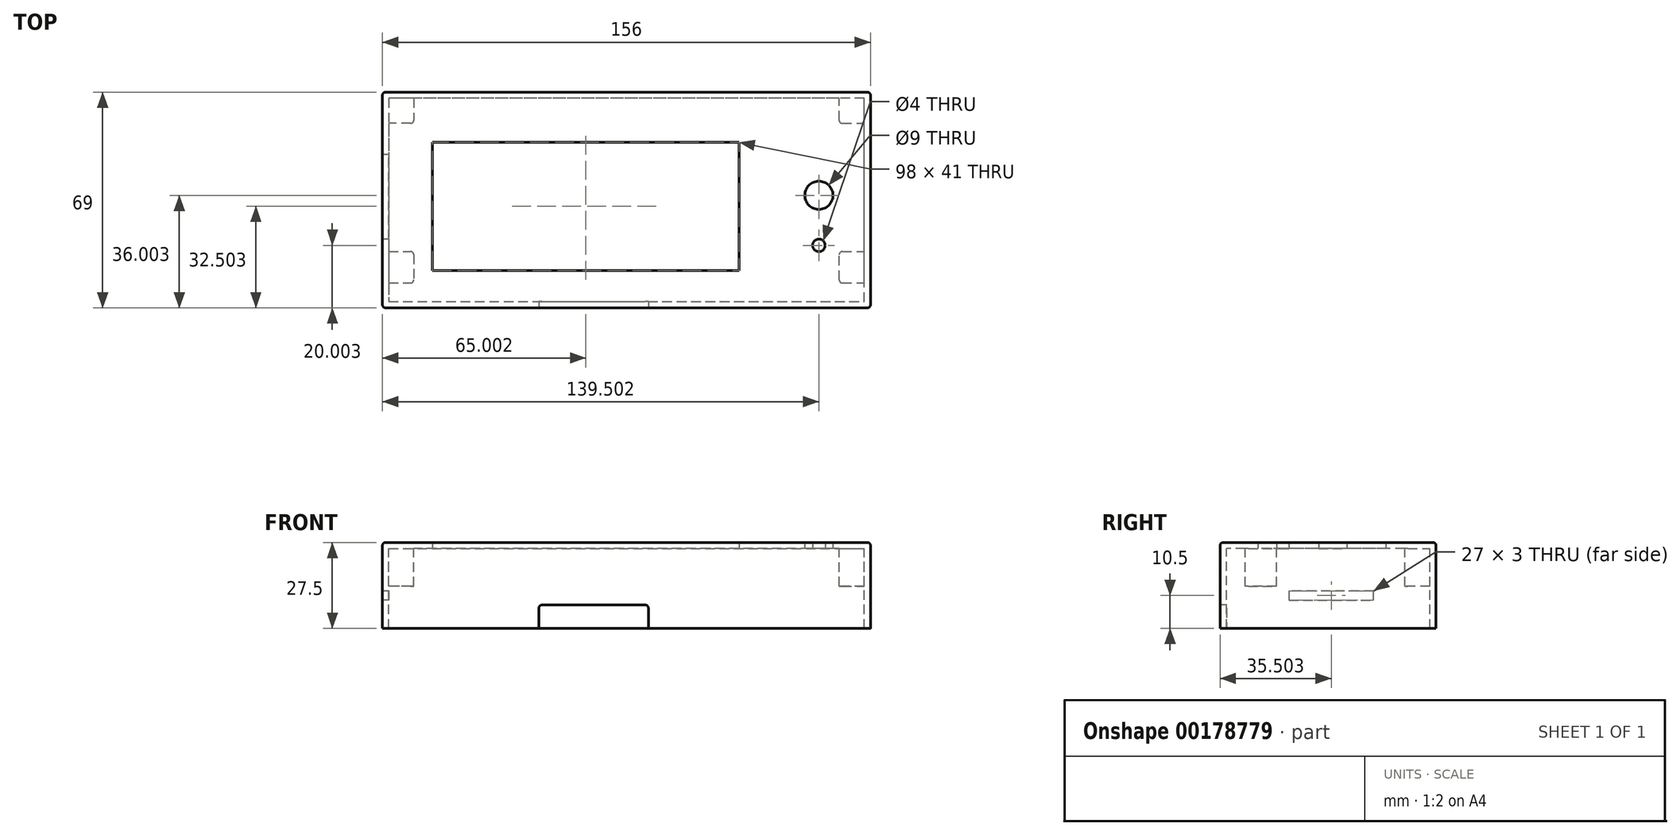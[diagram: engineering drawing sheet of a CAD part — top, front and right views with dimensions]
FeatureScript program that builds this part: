
annotation { "Feature Type Name" : "Feature", "Feature Type Description" : "" }
export const myFeature = defineFeature(function(context is Context, id is Id, definition is map)
    precondition{}
    {
        {
            var Q0;
            Q0=qCreatedBy(makeId("Top.planeOp"),FACE);
            var sketch = newSketch(context, id + "F0", { "sketchPlane" : qUnion([Q0])});
            skLineSegment(sketch, "E0.0", {"start": v(87.7, -27.77) * mm, "end": v(87.7, 35.23) * mm, "construction": true});
            skPoint(sketch, "E1.centerSnap0", {"position": v(87.7, 3.73) * mm});
            skLineSegment(sketch, "E2.0", {"start": v(101.2, 15.23) * mm, "end": v(-48.8, 15.23) * mm, "construction": true});
            skLineSegment(sketch, "E3.0", {"start": v(101.2, -11.77) * mm, "end": v(-48.8, -11.77) * mm, "construction": true});
            skLineSegment(sketch, "E4.0", {"start": v(62.2, 22.23) * mm, "end": v(-35.8, 22.23) * mm});
            skLineSegment(sketch, "E4.1", {"start": v(62.2, -18.77) * mm, "end": v(62.2, 22.23) * mm});
            skLineSegment(sketch, "E4.2", {"start": v(-35.8, -18.77) * mm, "end": v(62.2, -18.77) * mm});
            skLineSegment(sketch, "E4.3", {"start": v(-35.8, 22.23) * mm, "end": v(-35.8, -18.77) * mm});
            skLineSegment(sketch, "E5.0", {"start": v(102.2, 36.23) * mm, "end": v(-49.8, 36.23) * mm});
            skLineSegment(sketch, "E5.1", {"start": v(102.2, -28.77) * mm, "end": v(102.2, 36.23) * mm});
            skLineSegment(sketch, "E5.2", {"start": v(-49.8, -28.77) * mm, "end": v(102.2, -28.77) * mm});
            skLineSegment(sketch, "E5.3", {"start": v(-49.8, 36.23) * mm, "end": v(-49.8, -28.77) * mm});
            skLineSegment(sketch, "E6", {"start": v(87.7, 5.23) * mm, "end": v(102.2, 5.23) * mm, "construction": true});
            skLineSegment(sketch, "E7.0", {"start": v(87.7, -10.77) * mm, "end": v(102.2, -10.77) * mm, "construction": true});
            skCircle(sketch, "E8", {"center": v(87.7, -10.77) * mm, "radius": 2 * mm});
            skLineSegment(sketch, "E9.0", {"start": v(104.2, 38.23) * mm, "end": v(-51.8, 38.23) * mm});
            skLineSegment(sketch, "E9.1", {"start": v(104.2, -30.77) * mm, "end": v(104.2, 38.23) * mm});
            skLineSegment(sketch, "E9.2", {"start": v(-51.8, -30.77) * mm, "end": v(104.2, -30.77) * mm});
            skLineSegment(sketch, "E9.3", {"start": v(-51.8, 38.23) * mm, "end": v(-51.8, -30.77) * mm});
            skLineSegment(sketch, "E10.0", {"start": v(-43.8, -12.77) * mm, "end": v(96.2, -12.77) * mm, "construction": true});
            skLineSegment(sketch, "E11.0", {"start": v(96.2, 30.23) * mm, "end": v(-43.8, 30.23) * mm, "construction": true});
            skLineSegment(sketch, "E12", {"start": v(96.2, -12.77) * mm, "end": v(102.2, -12.77) * mm});
            skLineSegment(sketch, "E13", {"start": v(-49.8, -12.77) * mm, "end": v(-43.8, -12.77) * mm});
            skLineSegment(sketch, "E14.0", {"start": v(94.2, 28.23) * mm, "end": v(94.2, 36.23) * mm});
            skLineSegment(sketch, "E14.1", {"start": v(94.2, 28.23) * mm, "end": v(102.2, 28.23) * mm});
            skLineSegment(sketch, "E15.0", {"start": v(94.2, -22.77) * mm, "end": v(94.2, -12.77) * mm});
            skLineSegment(sketch, "E16", {"start": v(96.2, -12.77) * mm, "end": v(94.2, -12.77) * mm});
            skLineSegment(sketch, "E17.0", {"start": v(96.2, -22.77) * mm, "end": v(102.2, -22.77) * mm});
            skLineSegment(sketch, "E18.trimOffspring", {"start": v(94.2, -22.77) * mm, "end": v(96.2, -22.77) * mm});
            skLineSegment(sketch, "E19.0", {"start": v(-41.8, -12.77) * mm, "end": v(-41.8, -22.77) * mm});
            skLineSegment(sketch, "E20.0", {"start": v(-49.8, -22.77) * mm, "end": v(-43.8, -22.77) * mm});
            skLineSegment(sketch, "E21", {"start": v(-43.8, -12.77) * mm, "end": v(-41.8, -12.77) * mm});
            skLineSegment(sketch, "E22", {"start": v(-43.8, -22.77) * mm, "end": v(-41.8, -22.77) * mm});
            skLineSegment(sketch, "E23.0", {"start": v(-41.8, 28.23) * mm, "end": v(-49.8, 28.23) * mm});
            skLineSegment(sketch, "E23.1", {"start": v(-41.8, 36.23) * mm, "end": v(-41.8, 28.23) * mm});
            skCircle(sketch, "E24", {"center": v(87.7, 5.23) * mm, "radius": 4.5 * mm});
            skSolve(sketch);
        }
        {
            var Q0;
            Q0=makeQuery(id+"F0.imprint","IMPRINT",FACE,{"disambiguationData":[TD([[makeQuery(id+"F0.imprint","IMPRINT",EDGE,{"derivedFrom":sQuery(id+"F0.wireOp",EDGE,"E1")}),-1.0]])]});
            var Q1;
            {var subQ0=sQuery(id+"F0.wireOp",EDGE,"E5.3");Q1=makeQuery(id+"F0.imprint","IMPRINT",FACE,{"disambiguationData":[TD([[makeQuery(id+"F0.imprint","IMPRINT",EDGE,{"derivedFrom":subQ0}),1.0]])]});}
            var Q2;
            {var subQ0=sQuery(id+"F0.wireOp",EDGE,"E5.1");Q2=makeQuery(id+"F0.imprint","IMPRINT",FACE,{"disambiguationData":[TD([[makeQuery(id+"F0.imprint","IMPRINT",EDGE,{"derivedFrom":subQ0}),1.0]])]});}
            var Q3;
            {var subQ0=sQuery(id+"F0.wireOp",EDGE,"E5.1");Q3=makeQuery(id+"F0.imprint","IMPRINT",FACE,{"disambiguationData":[TD([[makeQuery(id+"F0.imprint","IMPRINT",EDGE,{"derivedFrom":subQ0}),-1.0]])]});}
            var Q4;
            {var subQ1=sQuery(id+"F0.wireOp",EDGE,"E13");Q4=makeQuery(id+"F0.imprint","IMPRINT",FACE,{"disambiguationData":[TD([[makeQuery(id+"F0.imprint","IMPRINT",EDGE,{"derivedFrom":subQ1}),-1.0]])]});}
            var Q5;
            {var subQ4=sQuery(id+"F0.wireOp",EDGE,"E23.0");Q5=makeQuery(id+"F0.imprint","IMPRINT",FACE,{"disambiguationData":[TD([[makeQuery(id+"F0.imprint","IMPRINT",EDGE,{"derivedFrom":subQ4}),-1.0]])]});}
            var Q6;
            {var subQ3=sQuery(id+"F0.wireOp",EDGE,"E14.0");Q6=makeQuery(id+"F0.imprint","IMPRINT",FACE,{"disambiguationData":[TD([[makeQuery(id+"F0.imprint","IMPRINT",EDGE,{"derivedFrom":subQ3}),-1.0]])]});}
            var Q7;
            {var subQ0=sQuery(id+"F0.wireOp",EDGE,"E12");Q7=makeQuery(id+"F0.imprint","IMPRINT",FACE,{"disambiguationData":[TD([[makeQuery(id+"F0.imprint","IMPRINT",EDGE,{"derivedFrom":subQ0}),-1.0]])]});}
            extrude(context, id + "F1", {"entities" : qUnion([Q0, Q1, Q2, Q3, Q4, Q5, Q6, Q7]), "depth" : 2 * mm});
        }
        {
            var Q0;
            {var subQ5=sQuery(id+"F0.wireOp",EDGE,"LqWD2sNj-Lfw8-2JLi-mVoA-2MaUUUqoJ69t");Q0=makeQuery(id+"F0.imprint","IMPRINT",FACE,{"disambiguationData":[TD([[makeQuery(id+"F0.imprint","IMPRINT",EDGE,{"derivedFrom":subQ5}),1.0]])]});}
            var Q1;
            {var subQ3=sQuery(id+"F0.wireOp",EDGE,"E12");Q1=makeQuery(id+"F0.imprint","IMPRINT",FACE,{"disambiguationData":[TD([[makeQuery(id+"F0.imprint","IMPRINT",EDGE,{"derivedFrom":subQ3}),-1.0]])]});}
            var Q2;
            {var subQ5=sQuery(id+"F0.wireOp",EDGE,"E13");Q2=makeQuery(id+"F0.imprint","IMPRINT",FACE,{"disambiguationData":[TD([[makeQuery(id+"F0.imprint","IMPRINT",EDGE,{"derivedFrom":subQ5}),-1.0]])]});}
            var Q3;
            {var subQ5=sQuery(id+"F0.wireOp",EDGE,"ybuCfW5r-dQPt-GAAb-xabZ-S6rsIlaVohmJ");Q3=makeQuery(id+"F0.imprint","IMPRINT",FACE,{"disambiguationData":[TD([[makeQuery(id+"F0.imprint","IMPRINT",EDGE,{"derivedFrom":subQ5}),-1.0]])]});}
            var Q4;
            {var subQ4=sQuery(id+"F0.wireOp",EDGE,"E23.0");Q4=makeQuery(id+"F0.imprint","IMPRINT",FACE,{"disambiguationData":[TD([[makeQuery(id+"F0.imprint","IMPRINT",EDGE,{"derivedFrom":subQ4}),-1.0]])]});}
            var Q5;
            {var subQ3=sQuery(id+"F0.wireOp",EDGE,"E14.0");Q5=makeQuery(id+"F0.imprint","IMPRINT",FACE,{"disambiguationData":[TD([[makeQuery(id+"F0.imprint","IMPRINT",EDGE,{"derivedFrom":subQ3}),-1.0]])]});}
            extrude(context, id + "F2", {"entities" : qUnion([Q0, Q1, Q2, Q3, Q4, Q5]), "operationType" : NewBodyOperationType.ADD, "oppositeDirection" : true, "depth" : (14 - 2) * mm});
        }
        {
            var Q0;
            Q0=makeQuery(id+"F0.imprint","IMPRINT",FACE,{"disambiguationData":[TD([[makeQuery(id+"F0.imprint","IMPRINT",EDGE,{"derivedFrom":sQuery(id+"F0.wireOp",EDGE,"E9.0")}),1.0]])]});
            extrude(context, id + "F3", {"entities" : qUnion([Q0]), "operationType" : NewBodyOperationType.ADD, "oppositeDirection" : true, "depth" : (15.5 + 10) * mm});
        }
        {
            var Q0;
            {var subQ0=sQuery(id+"F0.wireOp",EDGE,"E9.3");Q0=makeQuery(id+"F3.boolean.opBoolean","MERGE",FACE,{"derivedFrom":[makeQuery(id+"F1.opExtrude","SWEPT_FACE",FACE,{"disambiguationData":[OSD([subQ0])]}),makeQuery(id+"F3.opExtrude","SWEPT_FACE",FACE,{"disambiguationData":[OSD([subQ0])]})]});}
            var sketch = newSketch(context, id + "F4", { "sketchPlane" : qUnion([Q0])});
            skLineSegment(sketch, "E25.0", {"start": v(-18.23, 2) * mm, "end": v(-18.23, -25.5) * mm, "construction": true});
            skLineSegment(sketch, "E26.0", {"start": v(8.77, 2) * mm, "end": v(8.77, -25.5) * mm, "construction": true});
            skLineSegment(sketch, "E27.0", {"start": v(-38.23, -13.5) * mm, "end": v(30.77, -13.5) * mm, "construction": true});
            skLineSegment(sketch, "E28", {"start": v(-18.23, -13.5) * mm, "end": v(8.77, -13.5) * mm});
            skLineSegment(sketch, "E29", {"start": v(8.77, -13.5) * mm, "end": v(8.77, -16.5) * mm});
            skLineSegment(sketch, "E30", {"start": v(8.77, -16.5) * mm, "end": v(-18.23, -16.5) * mm});
            skLineSegment(sketch, "E31", {"start": v(-18.23, -16.5) * mm, "end": v(-18.23, -13.5) * mm});
            skLineSegment(sketch, "E32.top", {"start": v(-18.23, -16.5) * mm, "end": v(8.77, -16.5) * mm});
            skLineSegment(sketch, "E32.left", {"start": v(-18.23, -13.5) * mm, "end": v(-18.23, -16.5) * mm});
            skSolve(sketch);
        }
        {
            var Q0;
            Q0=makeQuery(id+"F4.imprint","IMPRINT",FACE,{"disambiguationData":[TD([[makeQuery(id+"F4.imprint","IMPRINT",EDGE,{"derivedFrom":sQuery(id+"F4.wireOp",EDGE,"E28")}),-1.0]])]});
            extrude(context, id + "F5", {"entities" : qUnion([Q0]), "operationType" : NewBodyOperationType.REMOVE, "oppositeDirection" : true, "depth" : 2 * mm});
        }
        {
            var Q0;
            {var subQ0=sQuery(id+"F0.wireOp",EDGE,"E9.2");Q0=makeQuery(id+"F3.boolean.opBoolean","MERGE",FACE,{"derivedFrom":[makeQuery(id+"F1.opExtrude","SWEPT_FACE",FACE,{"disambiguationData":[OSD([subQ0])]}),makeQuery(id+"F3.opExtrude","SWEPT_FACE",FACE,{"disambiguationData":[OSD([subQ0])]})]});}
            var sketch = newSketch(context, id + "F6", { "sketchPlane" : qUnion([Q0])});
            skLineSegment(sketch, "E33.0", {"start": v(-1.8, 2) * mm, "end": v(-1.8, -25.5) * mm, "construction": true});
            skLineSegment(sketch, "E34.0", {"start": v(33.2, 2) * mm, "end": v(33.2, -25.5) * mm, "construction": true});
            skLineSegment(sketch, "E35.0", {"start": v(-51.8, -18) * mm, "end": v(104.2, -18) * mm, "construction": true});
            skLineSegment(sketch, "E36.bottom", {"start": v(-1.8, -18) * mm, "end": v(33.2, -18) * mm});
            skLineSegment(sketch, "E36.top", {"start": v(-1.8, -25.5) * mm, "end": v(33.2, -25.5) * mm});
            skLineSegment(sketch, "E36.left", {"start": v(-1.8, -18) * mm, "end": v(-1.8, -25.5) * mm});
            skLineSegment(sketch, "E36.right", {"start": v(33.2, -18) * mm, "end": v(33.2, -25.5) * mm});
            skSolve(sketch);
        }
        {
            var Q0;
            Q0=makeQuery(id+"F6.imprint","IMPRINT",FACE,{"disambiguationData":[TD([[makeQuery(id+"F6.imprint","IMPRINT",EDGE,{"derivedFrom":sQuery(id+"F6.wireOp",EDGE,"E36.bottom")}),-1.0]])]});
            extrude(context, id + "F7", {"entities" : qUnion([Q0]), "operationType" : NewBodyOperationType.REMOVE, "oppositeDirection" : true, "depth" : 2 * mm});
        }
        {
            var Q0;
            {var subQ0=sQuery(id+"F0.wireOp",EDGE,"E9.3");var subQ1=sQuery(id+"F0.wireOp",EDGE,"E9.2");Q0=makeQuery(id+"F3.boolean.opBoolean","MERGE",EDGE,{"derivedFrom":[makeQuery(id+"F1.opExtrude","SWEPT_EDGE",EDGE,{"disambiguationData":[OSD([subQ1,subQ0])]}),makeQuery(id+"F3.opExtrude","SWEPT_EDGE",EDGE,{"disambiguationData":[OSD([subQ1,subQ0])]})]});}
            var Q1;
            Q1=makeQuery(id+"F1.opExtrude","CAP_EDGE",EDGE,{"disambiguationData":[OSD([sQuery(id+"F0.wireOp",EDGE,"E9.2")])],"isStart":false});
            var Q2;
            {var subQ0=sQuery(id+"F0.wireOp",EDGE,"E9.2");var subQ1=sQuery(id+"F0.wireOp",EDGE,"E9.1");Q2=makeQuery(id+"F3.boolean.opBoolean","MERGE",EDGE,{"derivedFrom":[makeQuery(id+"F1.opExtrude","SWEPT_EDGE",EDGE,{"disambiguationData":[OSD([subQ1,subQ0])]}),makeQuery(id+"F3.opExtrude","SWEPT_EDGE",EDGE,{"disambiguationData":[OSD([subQ1,subQ0])]})]});}
            var Q3;
            Q3=makeQuery(id+"F1.opExtrude","CAP_EDGE",EDGE,{"disambiguationData":[OSD([sQuery(id+"F0.wireOp",EDGE,"E9.1")])],"isStart":false});
            var Q4;
            {var subQ0=sQuery(id+"F0.wireOp",EDGE,"E9.1");var subQ1=sQuery(id+"F0.wireOp",EDGE,"E9.0");Q4=makeQuery(id+"F3.boolean.opBoolean","MERGE",EDGE,{"derivedFrom":[makeQuery(id+"F1.opExtrude","SWEPT_EDGE",EDGE,{"disambiguationData":[OSD([subQ1,subQ0])]}),makeQuery(id+"F3.opExtrude","SWEPT_EDGE",EDGE,{"disambiguationData":[OSD([subQ1,subQ0])]})]});}
            var Q5;
            Q5=makeQuery(id+"F1.opExtrude","CAP_EDGE",EDGE,{"disambiguationData":[OSD([sQuery(id+"F0.wireOp",EDGE,"E9.0")])],"isStart":false});
            var Q6;
            {var subQ0=sQuery(id+"F0.wireOp",EDGE,"E9.3");var subQ1=sQuery(id+"F0.wireOp",EDGE,"E9.0");Q6=makeQuery(id+"F3.boolean.opBoolean","MERGE",EDGE,{"derivedFrom":[makeQuery(id+"F1.opExtrude","SWEPT_EDGE",EDGE,{"disambiguationData":[OSD([subQ1,subQ0])]}),makeQuery(id+"F3.opExtrude","SWEPT_EDGE",EDGE,{"disambiguationData":[OSD([subQ1,subQ0])]})]});}
            var Q7;
            Q7=makeQuery(id+"F2.opExtrude","SWEPT_EDGE",EDGE,{"disambiguationData":[OSD([sQuery(id+"F0.wireOp",EDGE,"d95ecad5-aaf0-46ce-bc26-c3553d7e4dae.0"),sQuery(id+"F0.wireOp",EDGE,"ybuCfW5r-dQPt-GAAb-xabZ-S6rsIlaVohmJ")])]});
            var Q8;
            Q8=makeQuery(id+"F2.opExtrude","SWEPT_EDGE",EDGE,{"disambiguationData":[OSD([sQuery(id+"F0.wireOp",EDGE,"ea918c8d-915d-4296-b256-6586ec142c67.0"),sQuery(id+"F0.wireOp",EDGE,"LqWD2sNj-Lfw8-2JLi-mVoA-2MaUUUqoJ69t")])]});
            var Q9;
            Q9=makeQuery(id+"F7.boolean.opBoolean","COPY",EDGE,{"derivedFrom":makeQuery(id+"F7.opExtrude","SWEPT_EDGE",EDGE,{"disambiguationData":[OSD([sQuery(id+"F6.wireOp",EDGE,"E36.bottom"),sQuery(id+"F6.wireOp",EDGE,"E36.left")])]})});
            var Q10;
            Q10=makeQuery(id+"F7.boolean.opBoolean","COPY",EDGE,{"derivedFrom":makeQuery(id+"F7.opExtrude","SWEPT_EDGE",EDGE,{"disambiguationData":[OSD([sQuery(id+"F6.wireOp",EDGE,"E36.bottom"),sQuery(id+"F6.wireOp",EDGE,"E36.right")])]})});
            var Q11;
            Q11=makeQuery(id+"F1.opExtrude","CAP_EDGE",EDGE,{"disambiguationData":[OSD([sQuery(id+"F0.wireOp",EDGE,"E9.3")])],"isStart":false});
            var Q12;
            Q12=makeQuery(id+"F2.opExtrude","SWEPT_EDGE",EDGE,{"disambiguationData":[OSD([sQuery(id+"F0.wireOp",EDGE,"E19.0"),sQuery(id+"F0.wireOp",EDGE,"E21")])]});
            var Q13;
            Q13=makeQuery(id+"F2.opExtrude","SWEPT_EDGE",EDGE,{"disambiguationData":[OSD([sQuery(id+"F0.wireOp",EDGE,"E19.0"),sQuery(id+"F0.wireOp",EDGE,"E22")])]});
            var Q14;
            Q14=makeQuery(id+"F2.opExtrude","SWEPT_EDGE",EDGE,{"disambiguationData":[OSD([sQuery(id+"F0.wireOp",EDGE,"E23.0"),sQuery(id+"F0.wireOp",EDGE,"E23.1")])]});
            var Q15;
            Q15=makeQuery(id+"F2.opExtrude","SWEPT_EDGE",EDGE,{"disambiguationData":[OSD([sQuery(id+"F0.wireOp",EDGE,"E15.0"),sQuery(id+"F0.wireOp",EDGE,"E16")])]});
            var Q16;
            Q16=makeQuery(id+"F2.opExtrude","SWEPT_EDGE",EDGE,{"disambiguationData":[OSD([sQuery(id+"F0.wireOp",EDGE,"E15.0"),sQuery(id+"F0.wireOp",EDGE,"E18.trimOffspring")])]});
            var Q17;
            Q17=makeQuery(id+"F2.opExtrude","SWEPT_EDGE",EDGE,{"disambiguationData":[OSD([sQuery(id+"F0.wireOp",EDGE,"E14.0"),sQuery(id+"F0.wireOp",EDGE,"E14.1")])]});
            var Q18;
            Q18=makeQuery(id+"F2.opExtrude","SWEPT_EDGE",EDGE,{"disambiguationData":[OSD([sQuery(id+"F0.wireOp",EDGE,"E5.1"),sQuery(id+"F0.wireOp",EDGE,"E12")])]});
            var Q19;
            Q19=makeQuery(id+"F2.opExtrude","SWEPT_EDGE",EDGE,{"disambiguationData":[OSD([sQuery(id+"F0.wireOp",EDGE,"E5.1"),sQuery(id+"F0.wireOp",EDGE,"E17.0")])]});
            var Q20;
            Q20=makeQuery(id+"F2.opExtrude","SWEPT_EDGE",EDGE,{"disambiguationData":[OSD([sQuery(id+"F0.wireOp",EDGE,"E5.1"),sQuery(id+"F0.wireOp",EDGE,"E14.1")])]});
            var Q21;
            Q21=makeQuery(id+"F2.opExtrude","SWEPT_EDGE",EDGE,{"disambiguationData":[OSD([sQuery(id+"F0.wireOp",EDGE,"E5.0"),sQuery(id+"F0.wireOp",EDGE,"E14.0")])]});
            var Q22;
            Q22=makeQuery(id+"F2.opExtrude","SWEPT_EDGE",EDGE,{"disambiguationData":[OSD([sQuery(id+"F0.wireOp",EDGE,"E5.3"),sQuery(id+"F0.wireOp",EDGE,"E13")])]});
            var Q23;
            Q23=makeQuery(id+"F2.opExtrude","SWEPT_EDGE",EDGE,{"disambiguationData":[OSD([sQuery(id+"F0.wireOp",EDGE,"E5.0"),sQuery(id+"F0.wireOp",EDGE,"E23.1")])]});
            var Q24;
            Q24=makeQuery(id+"F2.opExtrude","SWEPT_EDGE",EDGE,{"disambiguationData":[OSD([sQuery(id+"F0.wireOp",EDGE,"E5.3"),sQuery(id+"F0.wireOp",EDGE,"E23.0")])]});
            var Q25;
            Q25=makeQuery(id+"F2.opExtrude","SWEPT_EDGE",EDGE,{"disambiguationData":[OSD([sQuery(id+"F0.wireOp",EDGE,"E5.3"),sQuery(id+"F0.wireOp",EDGE,"E20.0")])]});
            fillet(context, id + "F8", {"entities" : qUnion([Q0, Q1, Q2, Q3, Q4, Q5, Q6, Q7, Q8, Q9, Q10, Q11, Q12, Q13, Q14, Q15, Q16, Q17, Q18, Q19, Q20, Q21, Q22, Q23, Q24, Q25]), "radius" : 1 * mm, "tangentPropagation" : true, "allowEdgeOverflow" : false});
        }
    });
